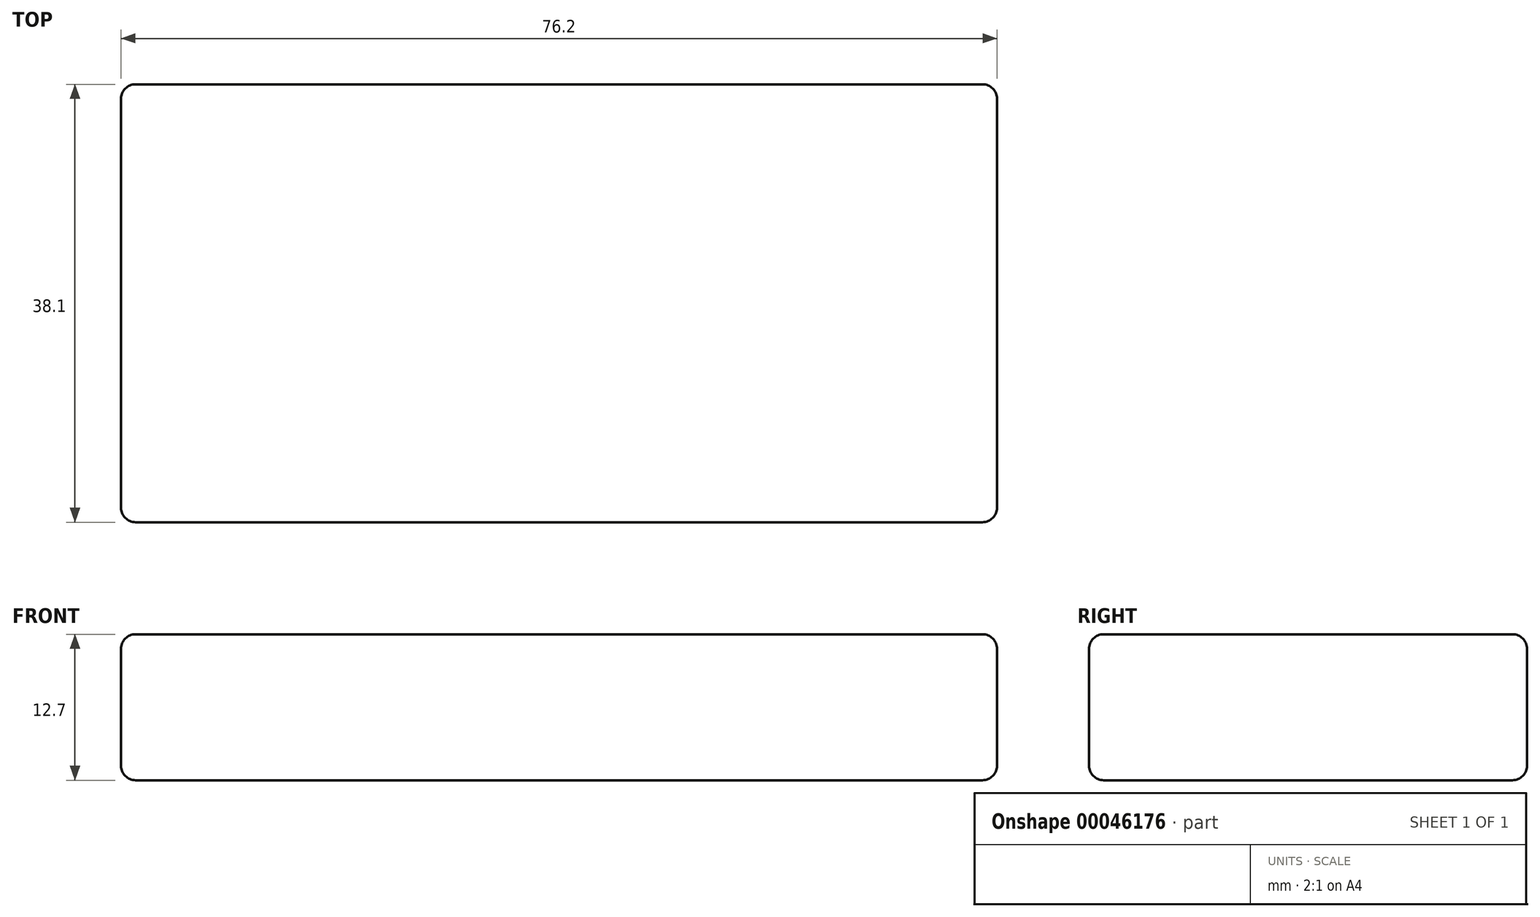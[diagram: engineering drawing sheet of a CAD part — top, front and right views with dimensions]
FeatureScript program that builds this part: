
annotation { "Feature Type Name" : "Feature", "Feature Type Description" : "" }
export const myFeature = defineFeature(function(context is Context, id is Id, definition is map)
    precondition{}
    {
        {
            var Q0;
            Q0=qCreatedBy(makeId("Top.planeOp"),FACE);
            var sketch = newSketch(context, id + "F0", { "sketchPlane" : qUnion([Q0])});
            skLineSegment(sketch, "E0.bottom", {"start": v(-38.1, 19.05) * mm, "end": v(38.1, 19.05) * mm});
            skLineSegment(sketch, "E0.top", {"start": v(-38.1, -19.05) * mm, "end": v(38.1, -19.05) * mm});
            skLineSegment(sketch, "E0.left", {"start": v(-38.1, 19.05) * mm, "end": v(-38.1, -19.05) * mm});
            skLineSegment(sketch, "E0.right", {"start": v(38.1, 19.05) * mm, "end": v(38.1, -19.05) * mm});
            skSolve(sketch);
        }
        {
            var Q0;
            Q0=makeQuery(id+"F0.imprint","IMPRINT",FACE,{"disambiguationData":[TD([[makeQuery(id+"F0.imprint","IMPRINT",EDGE,{"derivedFrom":sQuery(id+"F0.wireOp",EDGE,"E0.bottom")}),-1.0]])]});
            extrude(context, id + "F1", {"entities" : qUnion([Q0]), "depth" : 12.7 * mm});
        }
        {
            var Q0;
            Q0=makeQuery(id+"F1.opExtrude","CAP_EDGE",EDGE,{"disambiguationData":[OSD([sQuery(id+"F0.wireOp",EDGE,"E0.top")])],"isStart":false});
            var Q1;
            Q1=makeQuery(id+"F1.opExtrude","CAP_EDGE",EDGE,{"disambiguationData":[OSD([sQuery(id+"F0.wireOp",EDGE,"E0.right")])],"isStart":false});
            var Q2;
            Q2=makeQuery(id+"F1.opExtrude","CAP_EDGE",EDGE,{"disambiguationData":[OSD([sQuery(id+"F0.wireOp",EDGE,"E0.bottom")])],"isStart":false});
            var Q3;
            Q3=makeQuery(id+"F1.opExtrude","CAP_EDGE",EDGE,{"disambiguationData":[OSD([sQuery(id+"F0.wireOp",EDGE,"E0.left")])],"isStart":false});
            var Q4;
            Q4=makeQuery(id+"F1.opExtrude","CAP_EDGE",EDGE,{"disambiguationData":[OSD([sQuery(id+"F0.wireOp",EDGE,"E0.bottom")])],"isStart":true});
            var Q5;
            Q5=makeQuery(id+"F1.opExtrude","CAP_EDGE",EDGE,{"disambiguationData":[OSD([sQuery(id+"F0.wireOp",EDGE,"E0.left")])],"isStart":true});
            var Q6;
            Q6=makeQuery(id+"F1.opExtrude","CAP_EDGE",EDGE,{"disambiguationData":[OSD([sQuery(id+"F0.wireOp",EDGE,"E0.top")])],"isStart":true});
            var Q7;
            Q7=makeQuery(id+"F1.opExtrude","CAP_EDGE",EDGE,{"disambiguationData":[OSD([sQuery(id+"F0.wireOp",EDGE,"E0.right")])],"isStart":true});
            var Q8;
            Q8=makeQuery(id+"F1.opExtrude","SWEPT_EDGE",EDGE,{"disambiguationData":[OSD([sQuery(id+"F0.wireOp",EDGE,"E0.top"),sQuery(id+"F0.wireOp",EDGE,"E0.right")])]});
            var Q9;
            Q9=makeQuery(id+"F1.opExtrude","SWEPT_EDGE",EDGE,{"disambiguationData":[OSD([sQuery(id+"F0.wireOp",EDGE,"E0.bottom"),sQuery(id+"F0.wireOp",EDGE,"E0.right")])]});
            var Q10;
            Q10=makeQuery(id+"F1.opExtrude","SWEPT_EDGE",EDGE,{"disambiguationData":[OSD([sQuery(id+"F0.wireOp",EDGE,"E0.bottom"),sQuery(id+"F0.wireOp",EDGE,"E0.left")])]});
            var Q11;
            Q11=makeQuery(id+"F1.opExtrude","SWEPT_EDGE",EDGE,{"disambiguationData":[OSD([sQuery(id+"F0.wireOp",EDGE,"E0.top"),sQuery(id+"F0.wireOp",EDGE,"E0.left")])]});
            fillet(context, id + "F2", {"entities" : qUnion([Q0, Q1, Q2, Q3, Q4, Q5, Q6, Q7, Q8, Q9, Q10, Q11]), "radius" : 1.27 * mm, "tangentPropagation" : true, "allowEdgeOverflow" : false});
        }
    });
